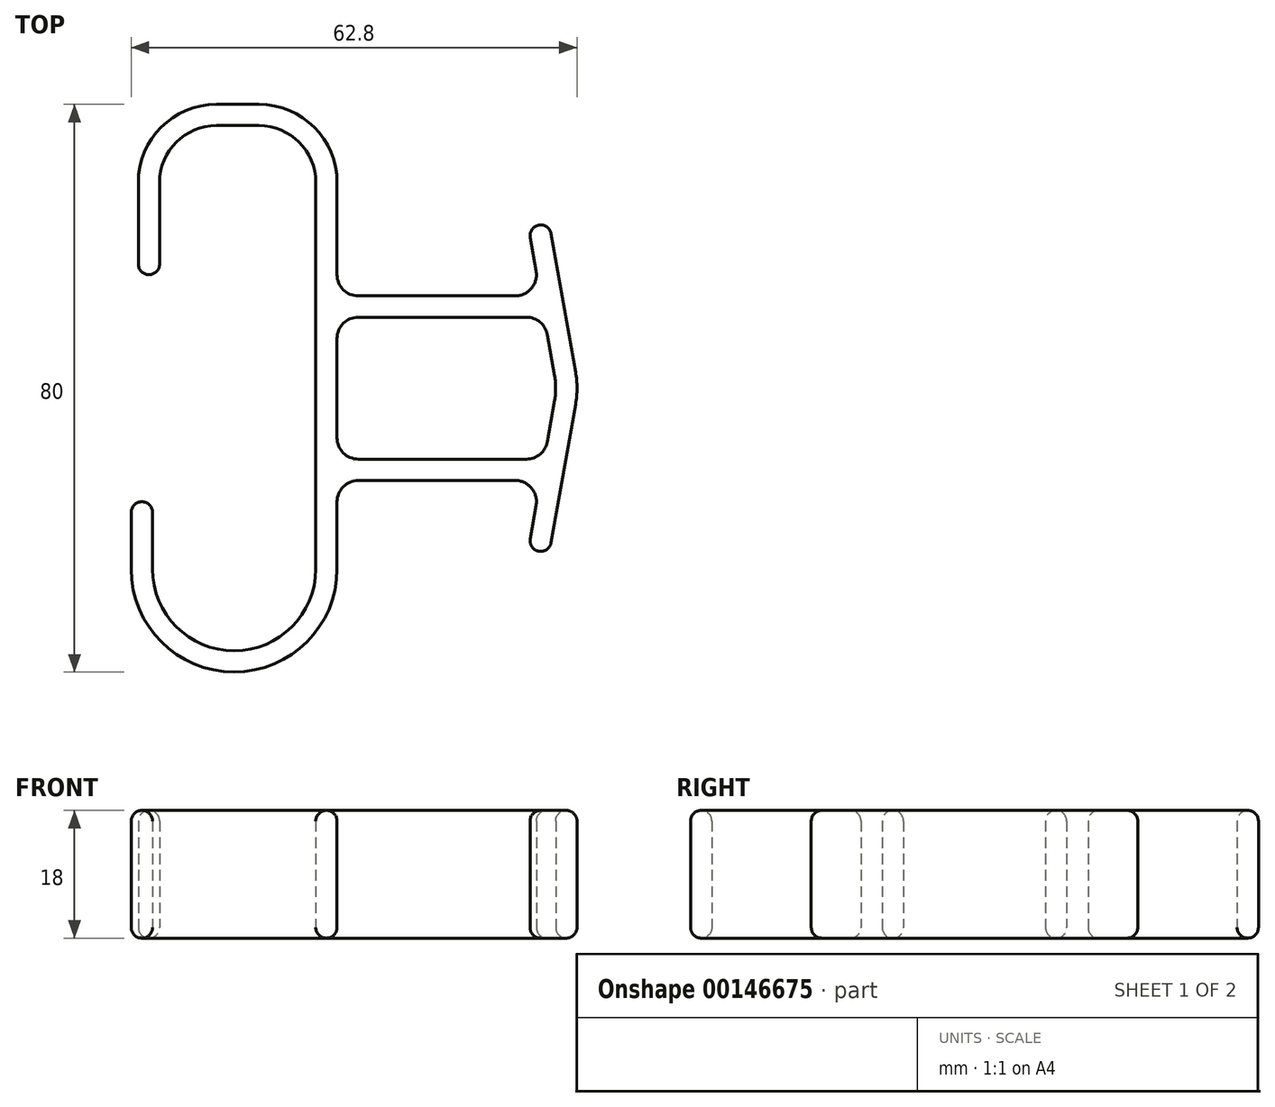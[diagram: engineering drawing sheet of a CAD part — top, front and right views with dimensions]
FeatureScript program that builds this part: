
annotation { "Feature Type Name" : "Feature", "Feature Type Description" : "" }
export const myFeature = defineFeature(function(context is Context, id is Id, definition is map)
    precondition{}
    {
        {
            var Q0;
            Q0=qCreatedBy(makeId("Top.planeOp"),FACE);
            var sketch = newSketch(context, id + "F0", { "sketchPlane" : qUnion([Q0])});
            skLineSegment(sketch, "E0.bottom", {"start": v(12, 37) * mm, "end": v(18, 37) * mm});
            skLineSegment(sketch, "E0.left", {"start": v(4, 29) * mm, "end": v(4, 17.5) * mm});
            skLineSegment(sketch, "E0.right", {"start": v(26, 29) * mm, "end": v(26, -25.5) * mm});
            skLineSegment(sketch, "E1", {"start": v(1, 17.5) * mm, "end": v(1, 29) * mm});
            skLineSegment(sketch, "E2", {"start": v(12, 40) * mm, "end": v(18, 40) * mm});
            skLineSegment(sketch, "E3", {"start": v(29, 29) * mm, "end": v(29, 16) * mm});
            skArc(sketch, "E4", {"start": v(1, 17.5) * mm, "mid": v(2.5, 16) * mm, "end": v(4, 17.5) * mm});
            skPoint(sketch, "E5.visualSharp", {"position": v(1, 40) * mm});
            skArc(sketch, "E5.filletArc", {"start": v(12, 40) * mm, "mid": v(4.22, 36.78) * mm, "end": v(1, 29) * mm});
            skArc(sketch, "E6.filletArc", {"start": v(29, 29) * mm, "mid": v(25.78, 36.78) * mm, "end": v(18, 40) * mm});
            skPoint(sketch, "E7.visualSharp", {"position": v(4, 37) * mm});
            skArc(sketch, "E7.filletArc", {"start": v(12, 37) * mm, "mid": v(6.34, 34.66) * mm, "end": v(4, 29) * mm});
            skPoint(sketch, "E8.visualSharp", {"position": v(26, 37) * mm});
            skArc(sketch, "E8.filletArc", {"start": v(26, 29) * mm, "mid": v(23.66, 34.66) * mm, "end": v(18, 37) * mm});
            skLineSegment(sketch, "E9", {"start": v(3, -25.5) * mm, "end": v(3, -17.5) * mm});
            skLineSegment(sketch, "E10", {"start": v(0, -17.5) * mm, "end": v(0, -25.5) * mm});
            skArc(sketch, "E11", {"start": v(3, -17.5) * mm, "mid": v(1.5, -16) * mm, "end": v(0, -17.5) * mm});
            skPoint(sketch, "E12.visualSharp", {"position": v(0, 0) * mm});
            skLineSegment(sketch, "E13", {"start": v(-9.45, 0) * mm, "end": v(29, 0) * mm, "construction": true});
            skArc(sketch, "E14", {"start": v(3, -25.5) * mm, "mid": v(14.5, -37) * mm, "end": v(26, -25.5) * mm});
            skArc(sketch, "E15", {"start": v(0, -25.5) * mm, "mid": v(14.5, -40) * mm, "end": v(29, -25.5) * mm});
            skLineSegment(sketch, "E16", {"start": v(32, 10) * mm, "end": v(55.67, 10) * mm});
            skLineSegment(sketch, "E17", {"start": v(56.2, 21.24) * mm, "end": v(57.04, 16.52) * mm});
            skLineSegment(sketch, "E18.0", {"start": v(32, 13) * mm, "end": v(54.09, 13) * mm});
            skLineSegment(sketch, "E19.0", {"start": v(59.16, 21.76) * mm, "end": v(62.6, 2.26) * mm});
            skArc(sketch, "E20", {"start": v(59.16, 21.76) * mm, "mid": v(57.43, 22.98) * mm, "end": v(56.2, 21.24) * mm});
            skLineSegment(sketch, "E21.trimOffspring", {"start": v(58.63, 7.52) * mm, "end": v(59.65, 1.74) * mm});
            skLineSegment(sketch, "E22.trimOffspring", {"start": v(29, 7) * mm, "end": v(29, -7) * mm});
            skPoint(sketch, "E23.visualSharp", {"position": v(29, 13) * mm});
            skArc(sketch, "E23.filletArc", {"start": v(29, 16) * mm, "mid": v(29.88, 13.88) * mm, "end": v(32, 13) * mm});
            skPoint(sketch, "E24.visualSharp", {"position": v(29, 10) * mm});
            skArc(sketch, "E24.filletArc", {"start": v(32, 10) * mm, "mid": v(29.88, 9.12) * mm, "end": v(29, 7) * mm});
            skPoint(sketch, "E25.visualSharp", {"position": v(57.66, 13) * mm});
            skArc(sketch, "E25.filletArc", {"start": v(54.09, 13) * mm, "mid": v(56.38, 14.07) * mm, "end": v(57.04, 16.52) * mm});
            skPoint(sketch, "E26.visualSharp", {"position": v(58.2, 10) * mm});
            skArc(sketch, "E26.filletArc", {"start": v(58.63, 7.52) * mm, "mid": v(57.6, 9.3) * mm, "end": v(55.67, 10) * mm});
            skArc(sketch, "E27.MirrorCS", {"start": v(29, -16) * mm, "mid": v(29.88, -13.88) * mm, "end": v(32, -13) * mm});
            skLineSegment(sketch, "E28.MirrorCS", {"start": v(32, -13) * mm, "end": v(54.09, -13) * mm});
            skArc(sketch, "E29.MirrorCS", {"start": v(54.09, -13) * mm, "mid": v(56.38, -14.07) * mm, "end": v(57.04, -16.52) * mm});
            skLineSegment(sketch, "E30.MirrorCS", {"start": v(56.2, -21.24) * mm, "end": v(57.04, -16.52) * mm});
            skArc(sketch, "E31.MirrorCS", {"start": v(59.16, -21.76) * mm, "mid": v(57.43, -22.98) * mm, "end": v(56.2, -21.24) * mm});
            skLineSegment(sketch, "E32.MirrorCS", {"start": v(59.16, -21.76) * mm, "end": v(62.6, -2.26) * mm});
            skLineSegment(sketch, "E33.MirrorCS", {"start": v(58.63, -7.52) * mm, "end": v(59.65, -1.74) * mm});
            skArc(sketch, "E34.MirrorCS", {"start": v(58.63, -7.52) * mm, "mid": v(57.6, -9.3) * mm, "end": v(55.67, -10) * mm});
            skLineSegment(sketch, "E35.MirrorCS", {"start": v(32, -10) * mm, "end": v(55.67, -10) * mm});
            skArc(sketch, "E36.MirrorCS", {"start": v(32, -10) * mm, "mid": v(29.88, -9.12) * mm, "end": v(29, -7) * mm});
            skLineSegment(sketch, "E37.trimOffspring", {"start": v(29, -16) * mm, "end": v(29, -25.5) * mm});
            skPoint(sketch, "E38.visualSharp", {"position": v(59.95, 0) * mm});
            skArc(sketch, "E38.filletArc", {"start": v(59.65, -1.74) * mm, "mid": v(59.8, 0) * mm, "end": v(59.65, 1.74) * mm});
            skPoint(sketch, "E39.visualSharp", {"position": v(63, 0) * mm});
            skArc(sketch, "E39.filletArc", {"start": v(62.6, -2.26) * mm, "mid": v(62.8, 0) * mm, "end": v(62.6, 2.26) * mm});
            skSolve(sketch);
        }
        {
            var Q0;
            Q0=makeQuery(id+"F0.imprint","IMPRINT",FACE,{"disambiguationData":[TD([[makeQuery(id+"F0.imprint","IMPRINT",EDGE,{"derivedFrom":sQuery(id+"F0.wireOp",EDGE,"E0.bottom")}),1.0]])]});
            extrude(context, id + "F1", {"entities" : qUnion([Q0]), "depth" : 18 * mm});
        }
        {
            var Q0;
            Q0=makeQuery(id+"F1.opExtrude","CAP_EDGE",EDGE,{"disambiguationData":[OSD([sQuery(id+"F0.wireOp",EDGE,"E0.left")])],"isStart":false});
            var Q1;
            Q1=makeQuery(id+"F1.opExtrude","CAP_EDGE",EDGE,{"disambiguationData":[OSD([sQuery(id+"F0.wireOp",EDGE,"E24.filletArc")])],"isStart":false});
            var Q2;
            Q2=makeQuery(id+"F1.opExtrude","CAP_EDGE",EDGE,{"disambiguationData":[OSD([sQuery(id+"F0.wireOp",EDGE,"E8.filletArc")])],"isStart":true});
            var Q3;
            Q3=makeQuery(id+"F1.opExtrude","CAP_EDGE",EDGE,{"disambiguationData":[OSD([sQuery(id+"F0.wireOp",EDGE,"E16")])],"isStart":true});
            fillet(context, id + "F2", {"entities" : qUnion([Q0, Q1, Q2, Q3]), "radius" : 1.5 * mm, "tangentPropagation" : true, "allowEdgeOverflow" : false});
        }
    });
